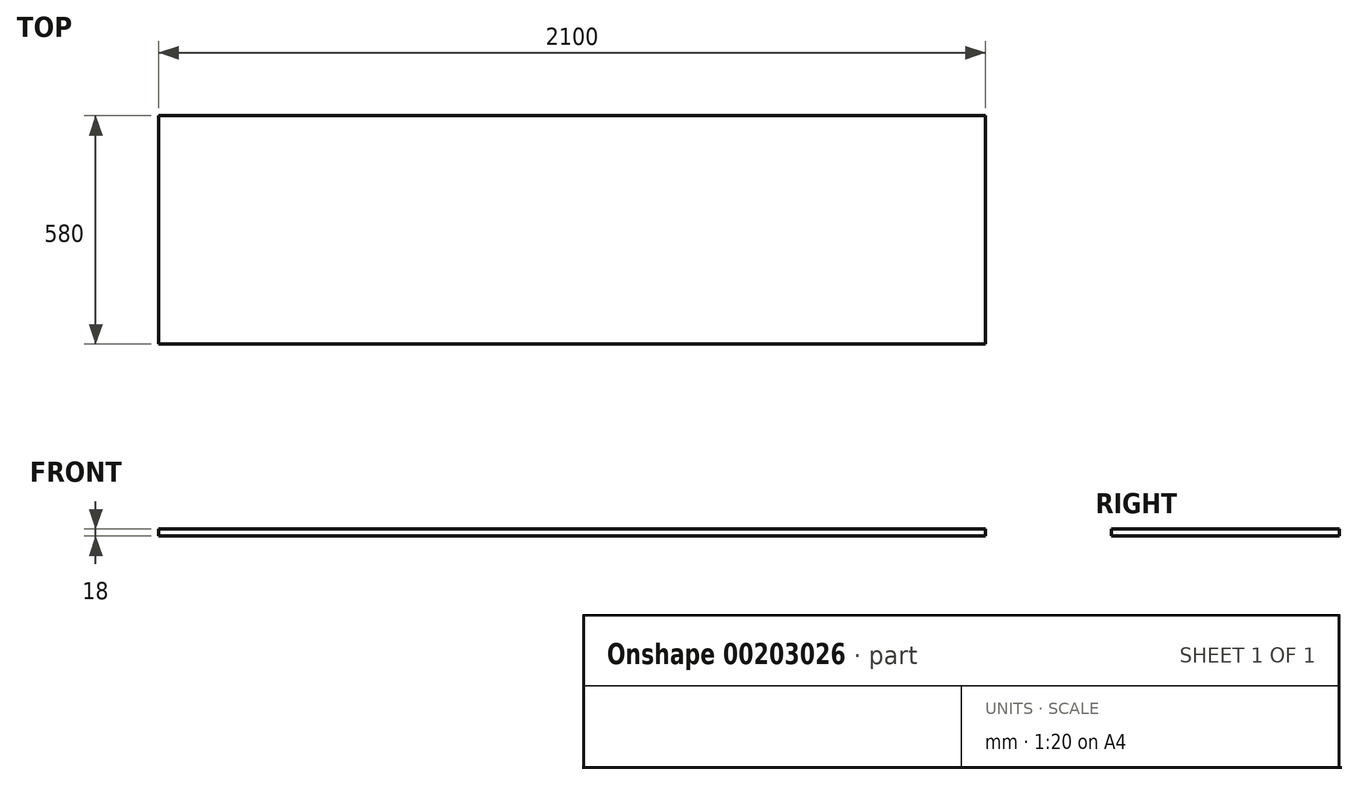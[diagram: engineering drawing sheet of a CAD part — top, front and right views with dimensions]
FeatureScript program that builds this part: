
annotation { "Feature Type Name" : "Feature", "Feature Type Description" : "" }
export const myFeature = defineFeature(function(context is Context, id is Id, definition is map)
    precondition{}
    {
        {
            var Q0;
            Q0=qCreatedBy(makeId("Top.planeOp"),FACE);
            var sketch = newSketch(context, id + "F0", { "sketchPlane" : qUnion([Q0])});
            skLineSegment(sketch, "E0.bottom", {"start": v(-1050, 290) * mm, "end": v(1050, 290) * mm});
            skLineSegment(sketch, "E0.top", {"start": v(-1050, -290) * mm, "end": v(1050, -290) * mm});
            skLineSegment(sketch, "E0.left", {"start": v(-1050, 290) * mm, "end": v(-1050, -290) * mm});
            skLineSegment(sketch, "E0.right", {"start": v(1050, 290) * mm, "end": v(1050, -290) * mm});
            skPoint(sketch, "E0.middle", {"position": v(0, 0) * mm});
            skSolve(sketch);
        }
        {
            var Q0;
            Q0=makeQuery(id+"F0.imprint","IMPRINT",FACE,{"disambiguationData":[TD([[makeQuery(id+"F0.imprint","IMPRINT",EDGE,{"derivedFrom":sQuery(id+"F0.wireOp",EDGE,"E0.bottom")}),-1.0]])]});
            extrude(context, id + "F1", {"entities" : qUnion([Q0]), "depth" : 18 * mm});
        }
    });
